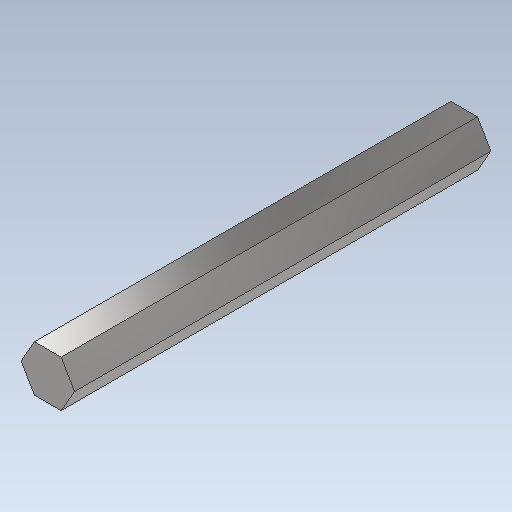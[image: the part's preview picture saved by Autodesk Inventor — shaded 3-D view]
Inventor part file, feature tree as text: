
AUTODESK INVENTOR PART (.ipt)
format: ipt  version: 2023 (Build 270158000, 158)  size: 96,768 bytes
history: native  units: in
note: dims shown in document units (in); Inventor stores cm internally (conversion verified against a paired STEP export)
features: extrude x1, sketch x1
ambient origin geometry x8: Origin, YZ Plane, XZ Plane, XY Plane, X Axis, Y Axis, Z Axis, Center Point
bodies: Solid1 (feature_tree)
feature tree (2):
  extrude  "Extrusion1"  Depth=4.5in TaperAngle=0.0deg
  sketch  "Sketch1"  dims[d0=0.5in d1=4.5in d2=0.0in]
